# Revit family: RN 55036 Optipress-Therm-Übergang
name_source: partatom
category: Rohrformteile
units: mm (PartAtom-declared; Revit-internal decimal feet)

## family parameters
Arbeitsebenenbasiert = Nein
Beim Laden mit Abzugskörper schneiden = Nein
Bemaßung runder Anschluss = Durchmesser verwenden
Gemeinsam genutzt = Nein
Immer vertikal = Ja
Teiletyp = Verbindung

## types (4) — shared parameters
1.010.00.2 Blattnummer der Richtlinie = 29
1.010.00.3 Ausgabedatum (Monat) der Richtlinie = 201308
1.010.00.4 Herstellername = R. Nussbaum AG
1.010.00.5 Revisionsdatum der Datei = 20190521
1.010.00.6 Webadresse des Herstellers = http://www.nussbaum.ch
1.100.00.4 Produktbezeichnung = Versorgung
1.110.00.2 Index = 1
1.110.00.4 Produktbezeichnung = Optipress-Therm
1.960/3L.00.8 Link (URL) = https://www.nussbaum.ch
29.700.00.4 Produktname = Optipress-Therm-Übergang, mit Einsteckende und Aussengewinde
29.700.00.5 Produktkennung = 2
29.700.00.6 Querschnittsform = 1
29.700.00.7 Nennweitensystem = DN
29.700.00.8 Nenndrucksystem = PN
29.710.02.4 Nenndruck = 16
29.710.02.5 max. zul. Überdruck [hPa] = 1600
29.710.02.7 max. zul. Dauer-Betriebsdruck [hPa] = 1600
29.710.02.9 max. zul. Dauer-Betriebstemperatur [°C] = 95
Connector Visibility = Nein
EnclosingSpace Visibility = Nein
Hersteller = R. Nussbaum AG

## per-type parameters (varying)
| type | 1.800.00.3 TGA-Nummer | 1.800.00.4 Kommentarfeld | 1.810.00.3 Hersteller-Bestellnummer | 1.810.00.4 DATANORM-Nummer | 1.810.00.5 StLB-Nummer | 1.810.00.6 GTIN-Nummer | 29.710.02.10 Formstück-Gewicht [kg] | 29.710.02.3 Benennung | CONNECTOR0_DIAMETER_dX_0r | CONNECTOR0_dX_01 | CONNECTOR0_ref_dX | CONNECTOR1_DIAMETER_dX_0r | CONNECTOR1_dX_00 | CONNECTOR1_dX_01 | CONNECTOR1_ref1_02 | CONNECTOR1_ref_dX | Modell | R. Nussbaum AG 55036.23 de Visibility | R. Nussbaum AG 55036.24 de Visibility | R. Nussbaum AG 55036.27 de Visibility | R. Nussbaum AG 55036.28 de Visibility | Typenkommentare |
| DN=25 | 01900100000000000000000000000000000000000000000023000000000000000004 | 55036.28, Optipress-Therm-Übergang, mit Einsteckende und Aussengewinde, DN=25, L=59, R=1 | 55036.28 | 55036.28 | 255.615 | 7612945685711 | 0.124 | Optipress-Therm-Übergang, mit Einsteckende und Aussengewinde, DN=25, L=59, R=1 | 25 mm  [stored 0.082021 ft] | 24 mm | 24 mm | 25 mm  [stored 0.082021 ft] | 42 mm | 59 mm | 59 mm | 42 mm | 55036.28 | Nein | Nein | Nein | Ja | Optipress-Therm-Übergang DN=25 |
| DN=20 | 01900100000000000000000000000000000000000000000023000000000000000003 | 55036.27, Optipress-Therm-Übergang, mit Einsteckende und Aussengewinde, DN=20, L=54, R=¾ | 55036.27 | 55036.27 | 255.614 | 7612945685704 | 0.086 | Optipress-Therm-Übergang, mit Einsteckende und Aussengewinde, DN=20, L=54, R=¾ | 20 mm | 24 mm | 24 mm | 20 mm | 39 mm  [stored 0.127953 ft] | 54 mm | 54 mm | 39 mm  [stored 0.127953 ft] | 55036.27 | Nein | Nein | Ja | Nein | Optipress-Therm-Übergang DN=20 |
| DN=15 | 01900100000000000000000000000000000000000000000023000000000000000002 | 55036.24, Optipress-Therm-Übergang, mit Einsteckende und Aussengewinde, DN=15, L=50, R=½ | 55036.24 | 55036.24 | 255.613 | 7612945685698 | 0.044 | Optipress-Therm-Übergang, mit Einsteckende und Aussengewinde, DN=15, L=50, R=½ | 15 mm  [stored 0.0492126 ft] | 22 mm | 22 mm | 15 mm  [stored 0.0492126 ft] | 37 mm | 50 mm | 50 mm | 37 mm | 55036.24 | Nein | Ja | Nein | Nein | Optipress-Therm-Übergang DN=15 |
| DN=12x15 | 01900100000000000000000000000000000000000000000023000000000000000001 | 55036.23, Optipress-Therm-Übergang, mit Einsteckende und Aussengewinde, DN=12x15, L=51, R=½ | 55036.23 | 55036.23 | 255.612 | 7612945685681 | 0.043 | Optipress-Therm-Übergang, mit Einsteckende und Aussengewinde, DN=12x15, L=51, R=½ | 12 mm  [stored 0.0393701 ft] | 22 mm | 22 mm | 15 mm  [stored 0.0492126 ft] | 38 mm | 51 mm | 51 mm | 38 mm | 55036.23 | Ja | Nein | Nein | Nein | Optipress-Therm-Übergang DN=12x15 |

note: [stored X ft] marks values corroborated as IEEE doubles in the binary element streams (Revit-internal decimal feet)

## geometry (parser evidence)
native form markers: Sweep x1
no freeform markers — native parametric forms only
